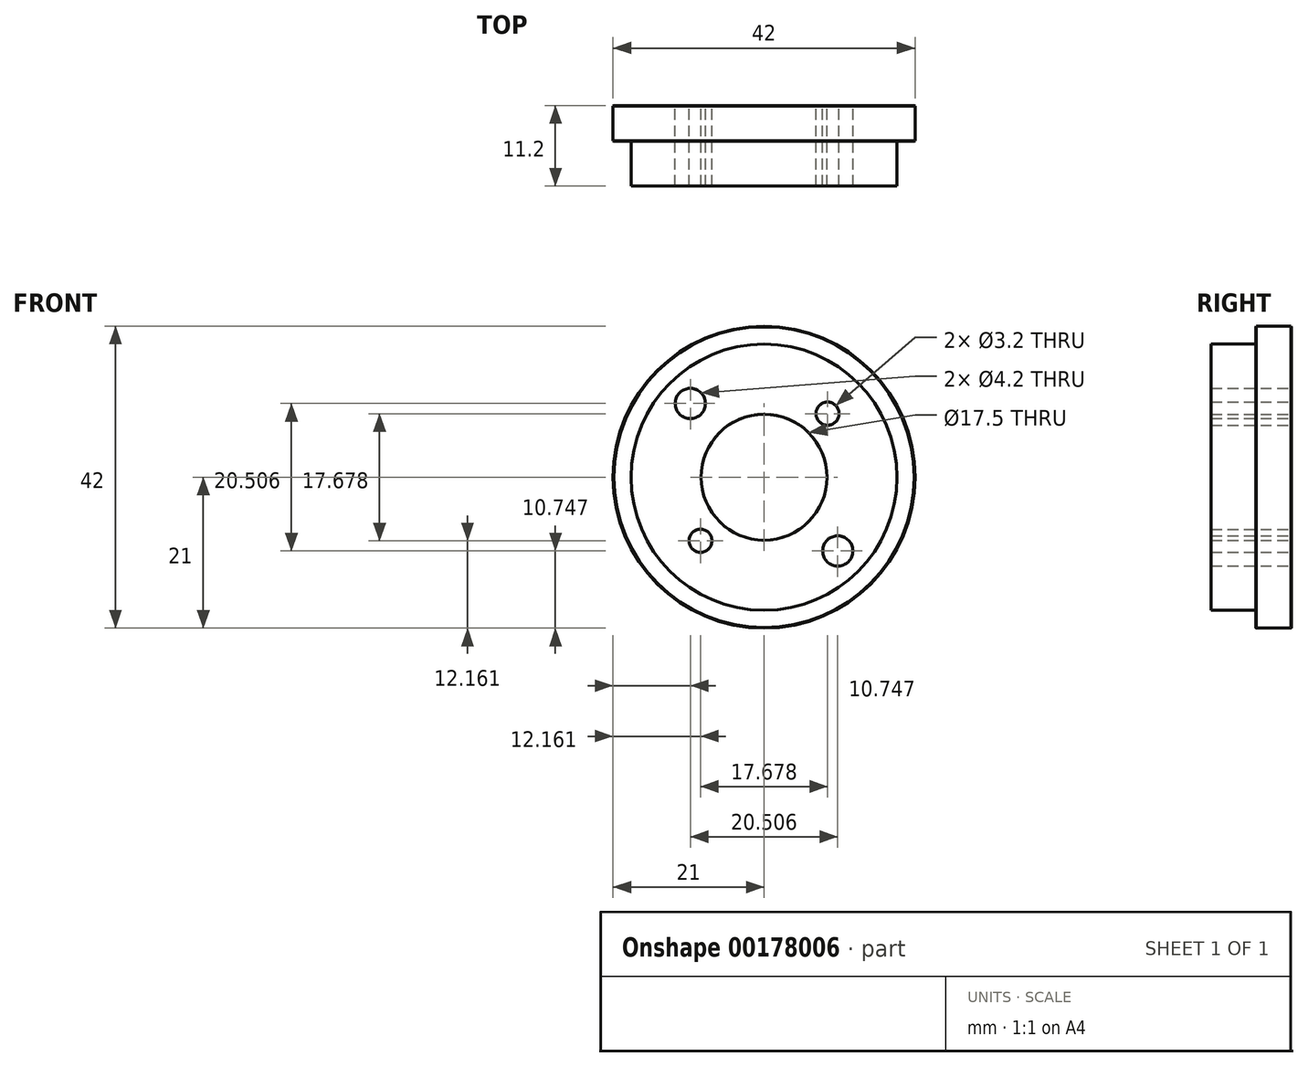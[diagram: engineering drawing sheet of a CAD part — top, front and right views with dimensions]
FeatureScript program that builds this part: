
annotation { "Feature Type Name" : "Feature", "Feature Type Description" : "" }
export const myFeature = defineFeature(function(context is Context, id is Id, definition is map)
    precondition{}
    {
        {
            var Q0;
            Q0=qCreatedBy(makeId("Front.planeOp"),FACE);
            var sketch = newSketch(context, id + "F0", { "sketchPlane" : qUnion([Q0])});
            skCircle(sketch, "E0", {"center": v(0, 0) * mm, "radius": 21 * mm});
            skSolve(sketch);
        }
        {
            var Q0;
            Q0=qSketchRegion(id+"F0",true);
            extrude(context, id + "F1", {"entities" : qUnion([Q0]), "oppositeDirection" : true, "depth" : 5 * mm});
        }
        {
            var Q0;
            Q0=qCreatedBy(makeId("Front.planeOp"),FACE);
            var sketch = newSketch(context, id + "F2", { "sketchPlane" : qUnion([Q0])});
            skCircle(sketch, "E1", {"center": v(0, 0) * mm, "radius": 18.5 * mm});
            skSolve(sketch);
        }
        {
            var Q0;
            Q0=qSketchRegion(id+"F2",true);
            extrude(context, id + "F3", {"entities" : qUnion([Q0]), "operationType" : NewBodyOperationType.ADD, "depth" : 6.2 * mm});
        }
        {
            var Q0;
            Q0=qCreatedBy(makeId("Front.planeOp"),FACE);
            var sketch = newSketch(context, id + "F4", { "sketchPlane" : qUnion([Q0])});
            skCircle(sketch, "E2", {"center": v(8.84, 8.84) * mm, "radius": 1.6 * mm});
            skCircle(sketch, "E3", {"center": v(-10.25, 10.25) * mm, "radius": 2.1 * mm});
            skCircle(sketch, "E4", {"center": v(-8.84, -8.84) * mm, "radius": 1.6 * mm});
            skCircle(sketch, "E5", {"center": v(10.25, -10.25) * mm, "radius": 2.1 * mm});
            skCircle(sketch, "E6", {"center": v(0, 0) * mm, "radius": 8.75 * mm});
            skLineSegment(sketch, "E7", {"start": v(-23.4, -23.4) * mm, "end": v(23.73, 23.73) * mm});
            skLineSegment(sketch, "E8", {"start": v(-25.41, 25.41) * mm, "end": v(25.28, -25.28) * mm});
            skSolve(sketch);
        }
        {
            var Q0;
            Q0=qSketchRegion(id+"F4",true);
            extrude(context, id + "F5", {"entities" : qUnion([Q0]), "operationType" : NewBodyOperationType.REMOVE, "depth" : 6.2 * mm, "hasSecondDirection" : true, "secondDirectionOppositeDirection" : true, "secondDirectionDepth" : 5 * mm});
        }
        {
            var Q0;
            Q0=makeQuery(id+"F1.opExtrude","CAP_FACE",FACE,{"disambiguationData":[OSD([sQuery(id+"F0.wireOp",EDGE,"E0")])],"isStart":false});
            var Q1;
            Q1=makeQuery(id+"F1.opExtrude","CAP_EDGE",EDGE,{"disambiguationData":[OSD([sQuery(id+"F0.wireOp",EDGE,"E0")])],"isStart":true});
            chamfer(context, id + "F6", {"entities" : qUnion([Q0, Q1]), "width" : 0.1 * mm, "tangentPropagation" : true});
        }
    });
